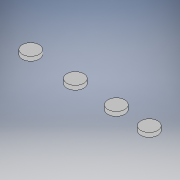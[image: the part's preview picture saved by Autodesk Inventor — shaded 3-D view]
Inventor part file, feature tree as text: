
AUTODESK INVENTOR PART (.ipt)
format: ipt  version: 2018 (Build 220112000, 112)  size: 98,304 bytes
history: native  units: in
note: dims shown in document units (in); Inventor stores cm internally (conversion verified against a paired STEP export)
features: extrude x1, sketch x1
ambient origin geometry x8: Origin, YZ Plane, XZ Plane, XY Plane, X Axis, Y Axis, Z Axis, Center Point
bodies: Body1 (feature_tree)
feature tree (2):
  extrude  "Extrusion4"  Depth=1.0in
  sketch  "Sketch1"  dims[d0=4.0in d12=1.5in d13=1.0in d14=0.0in]
